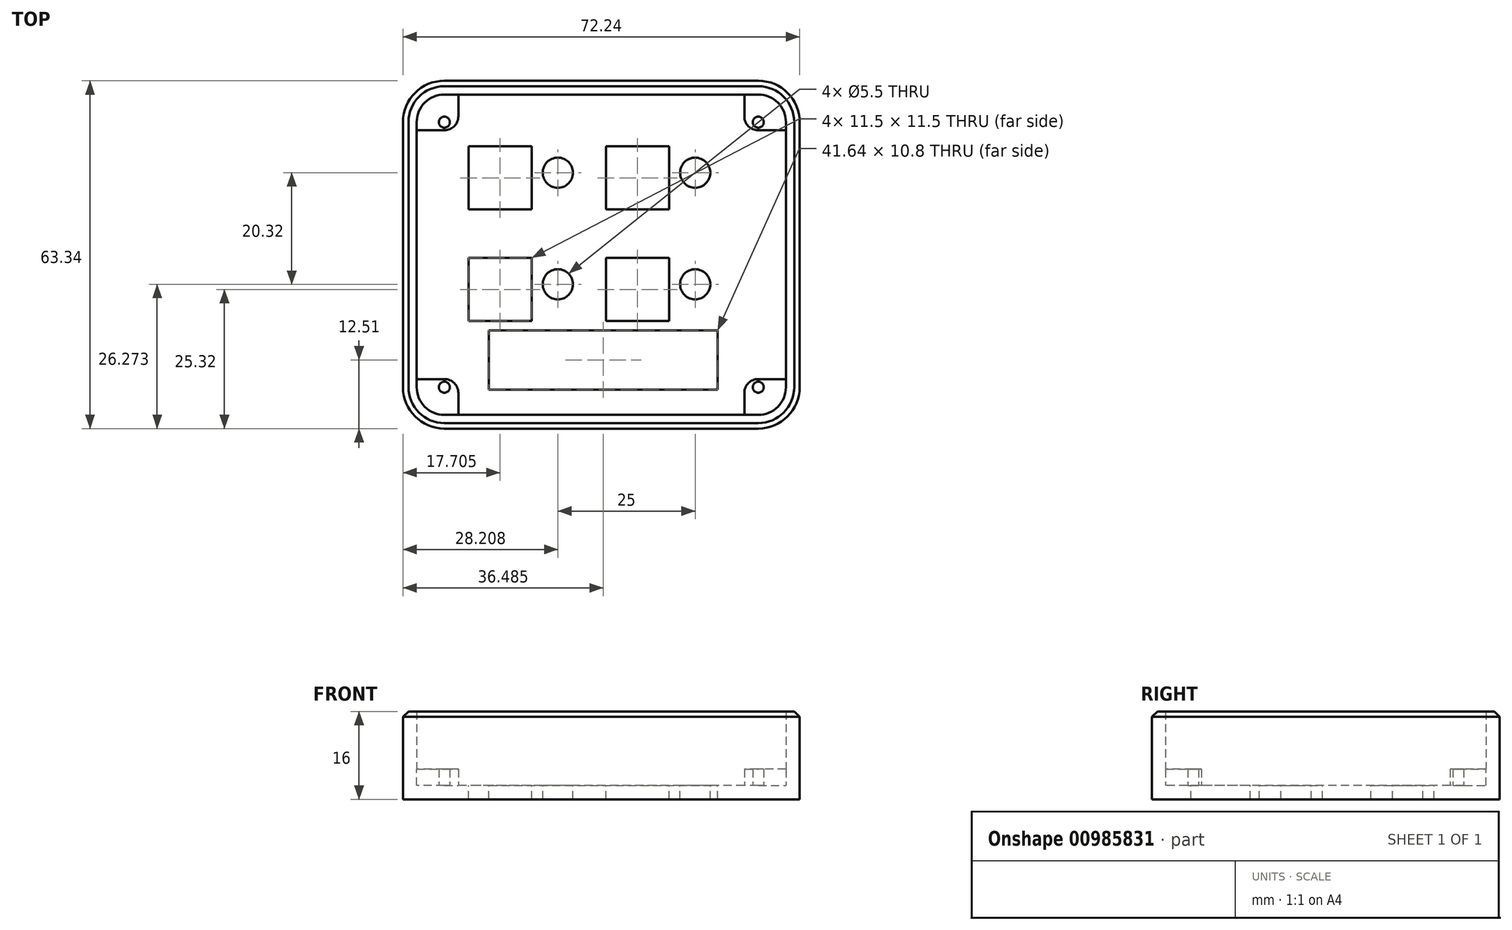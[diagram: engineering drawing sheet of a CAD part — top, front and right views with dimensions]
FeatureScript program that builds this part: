
annotation { "Feature Type Name" : "Feature", "Feature Type Description" : "" }
export const myFeature = defineFeature(function(context is Context, id is Id, definition is map)
    precondition{}
    {
        {
            var Q0;
            Q0=qCreatedBy(makeId("Top.planeOp"),FACE);
            var sketch = newSketch(context, id + "F0", { "sketchPlane" : qUnion([Q0])});
            skLineSegment(sketch, "E0.bottom", {"start": v(28.57, 31.67) * mm, "end": v(-28.58, 31.67) * mm});
            skLineSegment(sketch, "E0.top", {"start": v(28.58, -31.67) * mm, "end": v(-28.57, -31.67) * mm});
            skLineSegment(sketch, "E0.left", {"start": v(36.11, 24.13) * mm, "end": v(36.12, -24.13) * mm});
            skLineSegment(sketch, "E0.right", {"start": v(-36.12, 24.13) * mm, "end": v(-36.11, -24.13) * mm});
            skPoint(sketch, "E0.middle", {"position": v(0, 0) * mm});
            skPoint(sketch, "E1.visualSharp", {"position": v(-36.12, 31.67) * mm});
            skArc(sketch, "E1.filletArc", {"start": v(-28.58, 31.67) * mm, "mid": v(-33.9, 29.46) * mm, "end": v(-36.12, 24.13) * mm});
            skPoint(sketch, "E2.visualSharp", {"position": v(36.11, 31.67) * mm});
            skArc(sketch, "E2.filletArc", {"start": v(36.11, 24.13) * mm, "mid": v(33.9, 29.46) * mm, "end": v(28.57, 31.67) * mm});
            skPoint(sketch, "E3.visualSharp", {"position": v(36.12, -31.67) * mm});
            skArc(sketch, "E3.filletArc", {"start": v(28.58, -31.67) * mm, "mid": v(33.9, -29.46) * mm, "end": v(36.12, -24.13) * mm});
            skPoint(sketch, "E4.visualSharp", {"position": v(-36.11, -31.67) * mm});
            skArc(sketch, "E4.filletArc", {"start": v(-36.12, -24.13) * mm, "mid": v(-33.9, -29.46) * mm, "end": v(-28.57, -31.67) * mm});
            skCircle(sketch, "E5", {"center": v(-28.58, 24.13) * mm, "radius": 1 * mm});
            skCircle(sketch, "E6", {"center": v(28.57, 24.13) * mm, "radius": 1 * mm});
            skCircle(sketch, "E7", {"center": v(-28.57, -24.13) * mm, "radius": 1 * mm});
            skCircle(sketch, "E8", {"center": v(28.58, -24.13) * mm, "radius": 1 * mm});
            skLineSegment(sketch, "E9", {"start": v(-26.04, 31.67) * mm, "end": v(-26.04, 25.19) * mm});
            skLineSegment(sketch, "E10", {"start": v(-36.12, 22.65) * mm, "end": v(-28.58, 22.65) * mm});
            skPoint(sketch, "E11.visualSharp", {"position": v(-26.04, 22.65) * mm});
            skArc(sketch, "E11.filletArc", {"start": v(-28.58, 22.65) * mm, "mid": v(-26.78, 23.39) * mm, "end": v(-26.04, 25.19) * mm});
            skLineSegment(sketch, "E12.MirrorCS", {"start": v(26.04, 31.67) * mm, "end": v(26.04, 25.19) * mm});
            skArc(sketch, "E13.MirrorCS", {"start": v(28.58, 22.65) * mm, "mid": v(26.78, 23.39) * mm, "end": v(26.04, 25.19) * mm});
            skLineSegment(sketch, "E14.MirrorCS", {"start": v(36.12, 22.65) * mm, "end": v(28.58, 22.65) * mm});
            skLineSegment(sketch, "E15.MirrorCS", {"start": v(-26.04, -31.67) * mm, "end": v(-26.04, -25.19) * mm});
            skArc(sketch, "E16.MirrorCS", {"start": v(-28.58, -22.65) * mm, "mid": v(-26.78, -23.39) * mm, "end": v(-26.04, -25.19) * mm});
            skLineSegment(sketch, "E17.MirrorCS", {"start": v(-36.12, -22.65) * mm, "end": v(-28.58, -22.65) * mm});
            skLineSegment(sketch, "E18.MirrorCS", {"start": v(36.12, -22.65) * mm, "end": v(28.58, -22.65) * mm});
            skArc(sketch, "E19.MirrorCS", {"start": v(28.58, -22.65) * mm, "mid": v(26.78, -23.39) * mm, "end": v(26.04, -25.19) * mm});
            skLineSegment(sketch, "E20.MirrorCS", {"start": v(26.04, -31.67) * mm, "end": v(26.04, -25.19) * mm});
            skSolve(sketch);
        }
        {
            var Q0;
            {var subQ0=sQuery(id+"F0.wireOp",EDGE,"E2.filletArc");Q0=makeQuery(id+"F0.imprint","IMPRINT",FACE,{"disambiguationData":[TD([[makeQuery(id+"F0.imprint","IMPRINT",EDGE,{"derivedFrom":subQ0}),1.0]])]});}
            var Q1;
            {var subQ0=sQuery(id+"F0.wireOp",EDGE,"E1.filletArc");Q1=makeQuery(id+"F0.imprint","IMPRINT",FACE,{"disambiguationData":[TD([[makeQuery(id+"F0.imprint","IMPRINT",EDGE,{"derivedFrom":subQ0}),1.0]])]});}
            var Q2;
            {var subQ0=sQuery(id+"F0.wireOp",EDGE,"E3.filletArc");Q2=makeQuery(id+"F0.imprint","IMPRINT",FACE,{"disambiguationData":[TD([[makeQuery(id+"F0.imprint","IMPRINT",EDGE,{"derivedFrom":subQ0}),1.0]])]});}
            var Q3;
            {var subQ0=sQuery(id+"F0.wireOp",EDGE,"E4.filletArc");Q3=makeQuery(id+"F0.imprint","IMPRINT",FACE,{"disambiguationData":[TD([[makeQuery(id+"F0.imprint","IMPRINT",EDGE,{"derivedFrom":subQ0}),1.0]])]});}
            var Q4;
            {var subQ1=sQuery(id+"F0.wireOp",EDGE,"E9");Q4=makeQuery(id+"F0.imprint","IMPRINT",FACE,{"disambiguationData":[TD([[makeQuery(id+"F0.imprint","IMPRINT",EDGE,{"derivedFrom":subQ1}),1.0]])]});}
            var Q5;
            Q5=makeQuery(id+"F0.imprint","IMPRINT",FACE,{"disambiguationData":[TD([[makeQuery(id+"F0.imprint","IMPRINT",EDGE,{"derivedFrom":sQuery(id+"F0.wireOp",EDGE,"E5")}),1.0]])]});
            var Q6;
            Q6=makeQuery(id+"F0.imprint","IMPRINT",FACE,{"disambiguationData":[TD([[makeQuery(id+"F0.imprint","IMPRINT",EDGE,{"derivedFrom":sQuery(id+"F0.wireOp",EDGE,"E6")}),1.0]])]});
            var Q7;
            Q7=makeQuery(id+"F0.imprint","IMPRINT",FACE,{"disambiguationData":[TD([[makeQuery(id+"F0.imprint","IMPRINT",EDGE,{"derivedFrom":sQuery(id+"F0.wireOp",EDGE,"E8")}),1.0]])]});
            var Q8;
            Q8=makeQuery(id+"F0.imprint","IMPRINT",FACE,{"disambiguationData":[TD([[makeQuery(id+"F0.imprint","IMPRINT",EDGE,{"derivedFrom":sQuery(id+"F0.wireOp",EDGE,"E7")}),1.0]])]});
            extrude(context, id + "F1", {"entities" : qUnion([Q0, Q1, Q2, Q3, Q4, Q5, Q6, Q7, Q8]), "depth" : 16 * mm, "offsetDistance" : 25 * mm});
        }
        {
            var Q0;
            Q0=makeQuery(id+"F1.opExtrude","CAP_FACE",FACE,{"disambiguationData":[OSD([sQuery(id+"F0.wireOp",EDGE,"E0.bottom"),sQuery(id+"F0.wireOp",EDGE,"E0.top"),sQuery(id+"F0.wireOp",EDGE,"E0.left"),sQuery(id+"F0.wireOp",EDGE,"E0.right"),sQuery(id+"F0.wireOp",EDGE,"E1.filletArc"),sQuery(id+"F0.wireOp",EDGE,"E2.filletArc"),sQuery(id+"F0.wireOp",EDGE,"E3.filletArc"),sQuery(id+"F0.wireOp",EDGE,"E4.filletArc")])],"isStart":false});
            shell(context, id + "F2", {"entities" : qUnion([Q0]), "thickness" : 2.5 * mm});
        }
        {
            var Q0;
            {var subQ0=sQuery(id+"F0.wireOp",EDGE,"E4.filletArc");Q0=makeQuery(id+"F0.imprint","IMPRINT",FACE,{"disambiguationData":[TD([[makeQuery(id+"F0.imprint","IMPRINT",EDGE,{"derivedFrom":subQ0}),1.0]])]});}
            var Q1;
            {var subQ0=sQuery(id+"F0.wireOp",EDGE,"E3.filletArc");Q1=makeQuery(id+"F0.imprint","IMPRINT",FACE,{"disambiguationData":[TD([[makeQuery(id+"F0.imprint","IMPRINT",EDGE,{"derivedFrom":subQ0}),1.0]])]});}
            var Q2;
            {var subQ0=sQuery(id+"F0.wireOp",EDGE,"E2.filletArc");Q2=makeQuery(id+"F0.imprint","IMPRINT",FACE,{"disambiguationData":[TD([[makeQuery(id+"F0.imprint","IMPRINT",EDGE,{"derivedFrom":subQ0}),1.0]])]});}
            var Q3;
            {var subQ0=sQuery(id+"F0.wireOp",EDGE,"E1.filletArc");Q3=makeQuery(id+"F0.imprint","IMPRINT",FACE,{"disambiguationData":[TD([[makeQuery(id+"F0.imprint","IMPRINT",EDGE,{"derivedFrom":subQ0}),1.0]])]});}
            extrude(context, id + "F3", {"entities" : qUnion([Q0, Q1, Q2, Q3]), "operationType" : NewBodyOperationType.ADD, "depth" : 5.5 * mm, "offsetDistance" : 25 * mm});
        }
        {
            var Q0;
            {var subQ0=sQuery(id+"F0.wireOp",EDGE,"E0.bottom");var subQ1=sQuery(id+"F0.wireOp",EDGE,"E0.top");var subQ2=sQuery(id+"F0.wireOp",EDGE,"E0.left");var subQ3=sQuery(id+"F0.wireOp",EDGE,"E0.right");Q0=makeQuery(id+"F3.boolean.opBoolean","SPLIT",FACE,{"disambiguationData":[TD([makeQuery(id+"F2.opShell","OFFSET_FACE",FACE,{"disambiguationData":[OSD([subQ0])]})])],"derivedFrom":makeQuery(id+"F2.opShell","OFFSET_FACE",FACE,{"disambiguationData":[OSD([subQ0,subQ1,subQ2,subQ3,sQuery(id+"F0.wireOp",EDGE,"E1.filletArc"),sQuery(id+"F0.wireOp",EDGE,"E2.filletArc"),sQuery(id+"F0.wireOp",EDGE,"E3.filletArc"),sQuery(id+"F0.wireOp",EDGE,"E4.filletArc")])]})});}
            var sketch = newSketch(context, id + "F4", { "sketchPlane" : qUnion([Q0])});
            skLineSegment(sketch, "E21.bottom", {"start": v(-20.45, -13.76) * mm, "end": v(21.19, -13.76) * mm});
            skLineSegment(sketch, "E21.top", {"start": v(-20.45, -24.56) * mm, "end": v(21.19, -24.56) * mm});
            skLineSegment(sketch, "E21.left", {"start": v(-20.45, -13.76) * mm, "end": v(-20.45, -24.56) * mm});
            skLineSegment(sketch, "E21.right", {"start": v(21.19, -13.76) * mm, "end": v(21.19, -24.56) * mm});
            skLineSegment(sketch, "E22.bottom", {"start": v(-12.67, 8.22) * mm, "end": v(-24.17, 8.22) * mm});
            skLineSegment(sketch, "E22.top", {"start": v(-12.67, 19.72) * mm, "end": v(-24.17, 19.72) * mm});
            skLineSegment(sketch, "E22.left", {"start": v(-12.67, 8.22) * mm, "end": v(-12.67, 19.72) * mm});
            skLineSegment(sketch, "E22.right", {"start": v(-24.17, 8.22) * mm, "end": v(-24.17, 19.72) * mm});
            skPoint(sketch, "E22.middle", {"position": v(-18.42, 13.97) * mm});
            skCircle(sketch, "E23", {"center": v(-7.91, 14.92) * mm, "radius": 2.75 * mm});
            skLineSegment(sketch, "E24.0.1.0", {"start": v(-12.67, -0.6) * mm, "end": v(-24.17, -0.6) * mm});
            skLineSegment(sketch, "E24.0.1.1", {"start": v(-12.67, -12.1) * mm, "end": v(-12.67, -0.6) * mm});
            skLineSegment(sketch, "E24.0.1.2", {"start": v(-12.67, -12.1) * mm, "end": v(-24.17, -12.1) * mm});
            skPoint(sketch, "E24.0.1.3", {"position": v(-18.42, -6.35) * mm});
            skCircle(sketch, "E24.0.1.4", {"center": v(-7.91, -5.4) * mm, "radius": 2.75 * mm});
            skLineSegment(sketch, "E24.0.1.5", {"start": v(-24.17, -12.1) * mm, "end": v(-24.17, -0.6) * mm});
            skLineSegment(sketch, "E24.1.0.0", {"start": v(12.34, 19.72) * mm, "end": v(0.83, 19.72) * mm});
            skLineSegment(sketch, "E24.1.0.1", {"start": v(12.33, 8.22) * mm, "end": v(12.34, 19.72) * mm});
            skLineSegment(sketch, "E24.1.0.2", {"start": v(12.33, 8.22) * mm, "end": v(0.83, 8.22) * mm});
            skPoint(sketch, "E24.1.0.3", {"position": v(6.58, 13.97) * mm});
            skCircle(sketch, "E24.1.0.4", {"center": v(17.09, 14.92) * mm, "radius": 2.75 * mm});
            skLineSegment(sketch, "E24.1.0.5", {"start": v(0.83, 8.22) * mm, "end": v(0.83, 19.72) * mm});
            skLineSegment(sketch, "E24.1.1.0", {"start": v(12.34, -0.6) * mm, "end": v(0.83, -0.6) * mm});
            skLineSegment(sketch, "E24.1.1.1", {"start": v(12.33, -12.1) * mm, "end": v(12.34, -0.6) * mm});
            skLineSegment(sketch, "E24.1.1.2", {"start": v(12.33, -12.1) * mm, "end": v(0.83, -12.1) * mm});
            skPoint(sketch, "E24.1.1.3", {"position": v(6.58, -6.35) * mm});
            skCircle(sketch, "E24.1.1.4", {"center": v(17.09, -5.4) * mm, "radius": 2.75 * mm});
            skLineSegment(sketch, "E24.1.1.5", {"start": v(0.83, -12.1) * mm, "end": v(0.83, -0.6) * mm});
            skLineSegment(sketch, "E24.direction1", {"start": v(-24.17, 8.22) * mm, "end": v(0.83, 8.22) * mm, "construction": true});
            skLineSegment(sketch, "E24.direction2", {"start": v(-24.17, 8.22) * mm, "end": v(-24.17, -12.1) * mm, "construction": true});
            skSolve(sketch);
        }
        {
            var Q0;
            Q0=makeQuery(id+"F4.imprint","IMPRINT",FACE,{"disambiguationData":[TD([[makeQuery(id+"F4.imprint","IMPRINT",EDGE,{"derivedFrom":sQuery(id+"F4.wireOp",EDGE,"E21.bottom")}),-1.0]])]});
            var Q1;
            Q1=makeQuery(id+"F4.imprint","IMPRINT",FACE,{"disambiguationData":[TD([[makeQuery(id+"F4.imprint","IMPRINT",EDGE,{"derivedFrom":sQuery(id+"F4.wireOp",EDGE,"E24.1.1.4")}),1.0]])]});
            var Q2;
            Q2=makeQuery(id+"F4.imprint","IMPRINT",FACE,{"disambiguationData":[TD([[makeQuery(id+"F4.imprint","IMPRINT",EDGE,{"derivedFrom":sQuery(id+"F4.wireOp",EDGE,"E24.1.0.0")}),1.0]])]});
            var Q3;
            Q3=makeQuery(id+"F4.imprint","IMPRINT",FACE,{"disambiguationData":[TD([[makeQuery(id+"F4.imprint","IMPRINT",EDGE,{"derivedFrom":sQuery(id+"F4.wireOp",EDGE,"E24.1.0.4")}),1.0]])]});
            var Q4;
            Q4=makeQuery(id+"F4.imprint","IMPRINT",FACE,{"disambiguationData":[TD([[makeQuery(id+"F4.imprint","IMPRINT",EDGE,{"derivedFrom":sQuery(id+"F4.wireOp",EDGE,"E24.1.1.0")}),1.0]])]});
            var Q5;
            Q5=makeQuery(id+"F4.imprint","IMPRINT",FACE,{"disambiguationData":[TD([[makeQuery(id+"F4.imprint","IMPRINT",EDGE,{"derivedFrom":sQuery(id+"F4.wireOp",EDGE,"E24.0.1.0")}),1.0]])]});
            var Q6;
            Q6=makeQuery(id+"F4.imprint","IMPRINT",FACE,{"disambiguationData":[TD([[makeQuery(id+"F4.imprint","IMPRINT",EDGE,{"derivedFrom":sQuery(id+"F4.wireOp",EDGE,"E24.0.1.4")}),1.0]])]});
            var Q7;
            Q7=makeQuery(id+"F4.imprint","IMPRINT",FACE,{"disambiguationData":[TD([[makeQuery(id+"F4.imprint","IMPRINT",EDGE,{"derivedFrom":sQuery(id+"F4.wireOp",EDGE,"E22.bottom")}),-1.0]])]});
            var Q8;
            Q8=makeQuery(id+"F4.imprint","IMPRINT",FACE,{"disambiguationData":[TD([[makeQuery(id+"F4.imprint","IMPRINT",EDGE,{"derivedFrom":sQuery(id+"F4.wireOp",EDGE,"E23")}),1.0]])]});
            extrude(context, id + "F5", {"entities" : qUnion([Q0, Q1, Q2, Q3, Q4, Q5, Q6, Q7, Q8]), "operationType" : NewBodyOperationType.REMOVE, "endBound" : BoundingType.THROUGH_ALL, "oppositeDirection" : true, "depth" : 25 * mm, "offsetDistance" : 25 * mm});
        }
        {
            var Q0;
            Q0=makeQuery(id+"F1.opExtrude","CAP_EDGE",EDGE,{"disambiguationData":[OSD([sQuery(id+"F0.wireOp",EDGE,"E0.left")])],"isStart":false});
            chamfer(context, id + "F6", {"entities" : qUnion([Q0]), "width" : 1 * mm, "tangentPropagation" : true});
        }
    });
